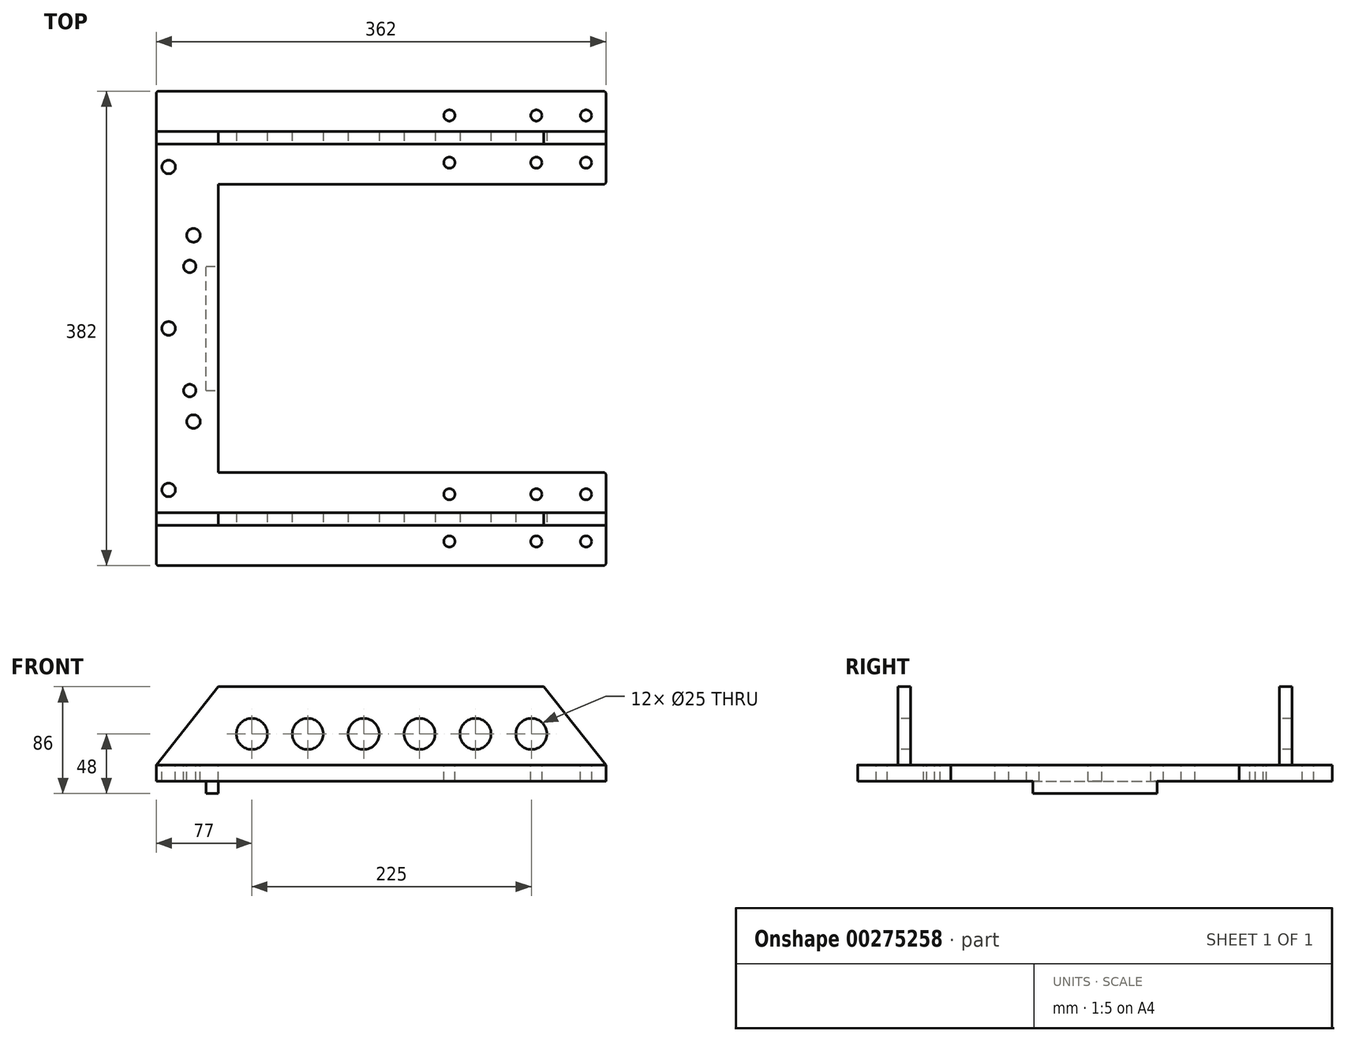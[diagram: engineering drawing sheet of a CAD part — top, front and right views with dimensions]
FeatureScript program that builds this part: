
annotation { "Feature Type Name" : "Feature", "Feature Type Description" : "" }
export const myFeature = defineFeature(function(context is Context, id is Id, definition is map)
    precondition{}
    {
        {
            var Q0;
            Q0=qCreatedBy(makeId("Top.planeOp"),FACE);
            var sketch = newSketch(context, id + "F0", { "sketchPlane" : qUnion([Q0])});
            skLineSegment(sketch, "E0", {"start": v(-299.03, 0) * mm, "end": v(319.03, 0) * mm, "construction": true});
            skLineSegment(sketch, "E1", {"start": v(0, 0) * mm, "end": v(0, 191) * mm});
            skLineSegment(sketch, "E2", {"start": v(0, 191) * mm, "end": v(362, 191) * mm});
            skLineSegment(sketch, "E3", {"start": v(362, 191) * mm, "end": v(362, 116) * mm});
            skLineSegment(sketch, "E4", {"start": v(362, 116) * mm, "end": v(0, 116) * mm});
            skLineSegment(sketch, "E5", {"start": v(50, 116) * mm, "end": v(50, 0) * mm});
            skLineSegment(sketch, "E6.MirrorCS", {"start": v(50, -116) * mm, "end": v(50, 0) * mm});
            skLineSegment(sketch, "E7.MirrorCS", {"start": v(0, 0) * mm, "end": v(0, -191) * mm});
            skLineSegment(sketch, "E8.MirrorCS", {"start": v(362, -116) * mm, "end": v(0, -116) * mm});
            skLineSegment(sketch, "E9.MirrorCS", {"start": v(0, -191) * mm, "end": v(362, -191) * mm});
            skLineSegment(sketch, "E10.MirrorCS", {"start": v(362, -191) * mm, "end": v(362, -116) * mm});
            skLineSegment(sketch, "E11", {"start": v(0, 158.5) * mm, "end": v(362, 158.5) * mm});
            skLineSegment(sketch, "E12", {"start": v(362, 148.5) * mm, "end": v(0, 148.5) * mm});
            skLineSegment(sketch, "E13.MirrorCS", {"start": v(362, -148.5) * mm, "end": v(0, -148.5) * mm});
            skLineSegment(sketch, "E14.MirrorCS", {"start": v(0, -158.5) * mm, "end": v(362, -158.5) * mm});
            skLineSegment(sketch, "E15", {"start": v(203.3, 171.5) * mm, "end": v(356.7, 171.5) * mm, "construction": true});
            skLineSegment(sketch, "E16", {"start": v(204.86, 133.5) * mm, "end": v(355.04, 133.5) * mm, "construction": true});
            skPoint(sketch, "E17", {"position": v(236, 171.5) * mm});
            skPoint(sketch, "E18", {"position": v(236, 133.5) * mm});
            skPoint(sketch, "E19", {"position": v(306, 171.5) * mm});
            skPoint(sketch, "E20", {"position": v(306, 133.5) * mm});
            skPoint(sketch, "E21", {"position": v(346, 171.5) * mm});
            skPoint(sketch, "E22", {"position": v(346, 133.5) * mm});
            skPoint(sketch, "E23", {"position": v(10, 130) * mm});
            skPoint(sketch, "E24", {"position": v(30, 75) * mm});
            skPoint(sketch, "E25", {"position": v(27, 50) * mm});
            skPoint(sketch, "E26", {"position": v(10, 0) * mm});
            skLineSegment(sketch, "E27", {"start": v(40, 0) * mm, "end": v(40, 50) * mm});
            skLineSegment(sketch, "E28", {"start": v(40, 50) * mm, "end": v(50, 50) * mm});
            skPoint(sketch, "E29.MirrorP", {"position": v(236, -171.5) * mm});
            skPoint(sketch, "E30.MirrorP", {"position": v(236, -133.5) * mm});
            skPoint(sketch, "E31.MirrorP", {"position": v(306, -171.5) * mm});
            skPoint(sketch, "E32.MirrorP", {"position": v(306, -133.5) * mm});
            skPoint(sketch, "E33.MirrorP", {"position": v(346, -171.5) * mm});
            skPoint(sketch, "E34.MirrorP", {"position": v(346, -133.5) * mm});
            skLineSegment(sketch, "E35.MirrorCS", {"start": v(40, 0) * mm, "end": v(40, -50) * mm});
            skPoint(sketch, "E36.MirrorP", {"position": v(27, -50) * mm});
            skLineSegment(sketch, "E37.MirrorCS", {"start": v(40, -50) * mm, "end": v(50, -50) * mm});
            skPoint(sketch, "E38.MirrorP", {"position": v(30, -75) * mm});
            skPoint(sketch, "E39.MirrorP", {"position": v(10, -130) * mm});
            skSolve(sketch);
        }
        {
            var Q0;
            Q0 = qSketchRegion(id + "F0", true);
            extrude(context, id + "F1", {"entities" : qUnion([Q0]), "oppositeDirection" : true, "depth" : 13 * mm});
        }
        {
            var Q0;
            Q0=makeQuery(id+"F0.imprint","IMPRINT",FACE,{"disambiguationData":[TD([[makeQuery(id+"F0.imprint","IMPRINT",EDGE,{"derivedFrom":sQuery(id+"F0.wireOp",EDGE,"E27")}),-1.0]])]});
            extrude(context, id + "F2", {"entities" : qUnion([Q0]), "operationType" : NewBodyOperationType.ADD, "oppositeDirection" : true, "depth" : (13 + 10) * mm});
        }
        {
            var Q0;
            {var subQ0=sQuery(id+"F0.wireOp",EDGE,"E11");Q0=makeQuery(id+"F0.imprint","IMPRINT",FACE,{"disambiguationData":[TD([[makeQuery(id+"F0.imprint","IMPRINT",EDGE,{"derivedFrom":subQ0}),-1.0]])]});}
            var Q1;
            {var subQ0=sQuery(id+"F0.wireOp",EDGE,"E13.MirrorCS");Q1=makeQuery(id+"F0.imprint","IMPRINT",FACE,{"disambiguationData":[TD([[makeQuery(id+"F0.imprint","IMPRINT",EDGE,{"derivedFrom":subQ0}),1.0]])]});}
            extrude(context, id + "F3", {"entities" : qUnion([Q0, Q1]), "operationType" : NewBodyOperationType.ADD, "depth" : 63 * mm});
        }
        {
            var Q0;
            Q0=sQuery(id+"F0.wireOp",VERTEX,"E17");
            var Q1;
            Q1=sQuery(id+"F0.wireOp",VERTEX,"E19");
            var Q2;
            Q2=sQuery(id+"F0.wireOp",VERTEX,"E21");
            var Q3;
            Q3=sQuery(id+"F0.wireOp",VERTEX,"E18");
            var Q4;
            Q4=sQuery(id+"F0.wireOp",VERTEX,"E20");
            var Q5;
            Q5=sQuery(id+"F0.wireOp",VERTEX,"E22");
            var Q6;
            Q6=sQuery(id+"F0.wireOp",VERTEX,"E29.MirrorP");
            var Q7;
            Q7=sQuery(id+"F0.wireOp",VERTEX,"E31.MirrorP");
            var Q8;
            Q8=sQuery(id+"F0.wireOp",VERTEX,"E33.MirrorP");
            var Q9;
            Q9=sQuery(id+"F0.wireOp",VERTEX,"E30.MirrorP");
            var Q10;
            Q10=sQuery(id+"F0.wireOp",VERTEX,"E32.MirrorP");
            var Q11;
            Q11=sQuery(id+"F0.wireOp",VERTEX,"E34.MirrorP");
            var Q12;
            Q12=makeQuery(id+"F1.opExtrude","SWEPT_BODY",BODY,{"disambiguationData":[OSD([sQuery(id+"F0.wireOp",EDGE,"E1"),sQuery(id+"F0.wireOp",EDGE,"E2"),sQuery(id+"F0.wireOp",EDGE,"E3"),sQuery(id+"F0.wireOp",EDGE,"E4"),sQuery(id+"F0.wireOp",EDGE,"E5"),sQuery(id+"F0.wireOp",EDGE,"E6.MirrorCS"),sQuery(id+"F0.wireOp",EDGE,"E7.MirrorCS"),sQuery(id+"F0.wireOp",EDGE,"E8.MirrorCS"),sQuery(id+"F0.wireOp",EDGE,"E9.MirrorCS"),sQuery(id+"F0.wireOp",EDGE,"E10.MirrorCS")])]});
            hole(context, id + "F4", {"style" : HoleStyle.SIMPLE, "endStyle" : HoleEndStyle.THROUGH, "holeDiameter" : 9 * mm, "tappedDepth" : 19.25 * mm, "tapClearance" : 3, "startFromSketch" : true, "locations" : qUnion([Q0, Q1, Q2, Q3, Q4, Q5, Q6, Q7, Q8, Q9, Q10, Q11]), "scope" : qUnion([Q12])});
        }
        {
            var Q0;
            Q0=sQuery(id+"F0.wireOp",VERTEX,"E23");
            var Q1;
            Q1=sQuery(id+"F0.wireOp",VERTEX,"E24");
            var Q2;
            Q2=sQuery(id+"F0.wireOp",VERTEX,"E39.MirrorP");
            var Q3;
            Q3=sQuery(id+"F0.wireOp",VERTEX,"E26");
            var Q4;
            Q4=sQuery(id+"F0.wireOp",VERTEX,"E38.MirrorP");
            var Q5;
            Q5=makeQuery(id+"F1.opExtrude","SWEPT_BODY",BODY,{"disambiguationData":[OSD([sQuery(id+"F0.wireOp",EDGE,"E1"),sQuery(id+"F0.wireOp",EDGE,"E2"),sQuery(id+"F0.wireOp",EDGE,"E3"),sQuery(id+"F0.wireOp",EDGE,"E4"),sQuery(id+"F0.wireOp",EDGE,"E5"),sQuery(id+"F0.wireOp",EDGE,"E6.MirrorCS"),sQuery(id+"F0.wireOp",EDGE,"E7.MirrorCS"),sQuery(id+"F0.wireOp",EDGE,"E8.MirrorCS"),sQuery(id+"F0.wireOp",EDGE,"E9.MirrorCS"),sQuery(id+"F0.wireOp",EDGE,"E10.MirrorCS")])]});
            hole(context, id + "F5", {"style" : HoleStyle.SIMPLE, "endStyle" : HoleEndStyle.THROUGH, "holeDiameter" : 11 * mm, "tappedDepth" : 19.25 * mm, "tapClearance" : 3, "startFromSketch" : true, "locations" : qUnion([Q0, Q1, Q2, Q3, Q4]), "scope" : qUnion([Q5])});
        }
        {
            var Q0;
            Q0=sQuery(id+"F0.wireOp",VERTEX,"E25");
            var Q1;
            Q1=sQuery(id+"F0.wireOp",VERTEX,"E36.MirrorP");
            var Q2;
            Q2=makeQuery(id+"F1.opExtrude","SWEPT_BODY",BODY,{"disambiguationData":[OSD([sQuery(id+"F0.wireOp",EDGE,"E1"),sQuery(id+"F0.wireOp",EDGE,"E2"),sQuery(id+"F0.wireOp",EDGE,"E3"),sQuery(id+"F0.wireOp",EDGE,"E4"),sQuery(id+"F0.wireOp",EDGE,"E5"),sQuery(id+"F0.wireOp",EDGE,"E6.MirrorCS"),sQuery(id+"F0.wireOp",EDGE,"E7.MirrorCS"),sQuery(id+"F0.wireOp",EDGE,"E8.MirrorCS"),sQuery(id+"F0.wireOp",EDGE,"E9.MirrorCS"),sQuery(id+"F0.wireOp",EDGE,"E10.MirrorCS")])]});
            hole(context, id + "F6", {"style" : HoleStyle.SIMPLE, "endStyle" : HoleEndStyle.THROUGH, "holeDiameter" : 10 * mm, "tappedDepth" : 19.25 * mm, "tapClearance" : 3, "startFromSketch" : true, "locations" : qUnion([Q0, Q1]), "scope" : qUnion([Q2])});
        }
        {
            var Q0;
            Q0=makeQuery(id+"F3.opExtrude","SWEPT_FACE",FACE,{"disambiguationData":[OSD([sQuery(id+"F0.wireOp",EDGE,"E14.MirrorCS")])]});
            var sketch = newSketch(context, id + "F7", { "sketchPlane" : qUnion([Q0])});
            skPoint(sketch, "E40", {"position": v(50, 63) * mm});
            skLineSegment(sketch, "E41.0", {"start": v(0, 63) * mm, "end": v(0, 0) * mm});
            skLineSegment(sketch, "E42.0", {"start": v(0, 63) * mm, "end": v(50, 63) * mm});
            skPoint(sketch, "E43.orphan", {"position": v(362, 63) * mm});
            skLineSegment(sketch, "E44", {"start": v(0, 0) * mm, "end": v(50, 63) * mm});
            skPoint(sketch, "E45", {"position": v(312, 63) * mm});
            skLineSegment(sketch, "E46", {"start": v(362, 0) * mm, "end": v(312, 63) * mm});
            skLineSegment(sketch, "E47.0", {"start": v(362, 63) * mm, "end": v(362, 0) * mm});
            skLineSegment(sketch, "E48.trimOffspring", {"start": v(312, 63) * mm, "end": v(362, 63) * mm});
            skLineSegment(sketch, "E49", {"start": v(-34.34, 25) * mm, "end": v(392.45, 25) * mm, "construction": true});
            skLineSegment(sketch, "E50.0", {"start": v(0, -13) * mm, "end": v(362, -13) * mm, "construction": true});
            skPoint(sketch, "E51", {"position": v(77, 25) * mm});
            skPoint(sketch, "E52", {"position": v(122, 25) * mm});
            skPoint(sketch, "E53", {"position": v(167, 25) * mm});
            skPoint(sketch, "E54", {"position": v(212, 25) * mm});
            skPoint(sketch, "E55", {"position": v(257, 25) * mm});
            skPoint(sketch, "E56", {"position": v(302, 25) * mm});
            skSolve(sketch);
        }
        {
            var Q0;
            Q0=makeQuery(id+"F7.imprint","IMPRINT",FACE,{"disambiguationData":[TD([[makeQuery(id+"F7.imprint","IMPRINT",EDGE,{"derivedFrom":sQuery(id+"F7.wireOp",EDGE,"E41.0")}),1.0]])]});
            var Q1;
            Q1=makeQuery(id+"F7.imprint","IMPRINT",FACE,{"disambiguationData":[TD([[makeQuery(id+"F7.imprint","IMPRINT",EDGE,{"derivedFrom":sQuery(id+"F7.wireOp",EDGE,"E46")}),-1.0]])]});
            extrude(context, id + "F8", {"entities" : qUnion([Q0, Q1]), "operationType" : NewBodyOperationType.REMOVE, "endBound" : BoundingType.THROUGH_ALL, "oppositeDirection" : true, "depth" : 25 * mm});
        }
        {
            var Q0;
            Q0=sQuery(id+"F7.wireOp",VERTEX,"E51");
            var Q1;
            Q1=sQuery(id+"F7.wireOp",VERTEX,"E52");
            var Q2;
            Q2=sQuery(id+"F7.wireOp",VERTEX,"E53");
            var Q3;
            Q3=sQuery(id+"F7.wireOp",VERTEX,"E54");
            var Q4;
            Q4=sQuery(id+"F7.wireOp",VERTEX,"E55");
            var Q5;
            Q5=sQuery(id+"F7.wireOp",VERTEX,"E56");
            var Q6;
            Q6=makeQuery(id+"F1.opExtrude","SWEPT_BODY",BODY,{"disambiguationData":[OSD([sQuery(id+"F0.wireOp",EDGE,"E1"),sQuery(id+"F0.wireOp",EDGE,"E2"),sQuery(id+"F0.wireOp",EDGE,"E3"),sQuery(id+"F0.wireOp",EDGE,"E4"),sQuery(id+"F0.wireOp",EDGE,"E5"),sQuery(id+"F0.wireOp",EDGE,"E6.MirrorCS"),sQuery(id+"F0.wireOp",EDGE,"E7.MirrorCS"),sQuery(id+"F0.wireOp",EDGE,"E8.MirrorCS"),sQuery(id+"F0.wireOp",EDGE,"E9.MirrorCS"),sQuery(id+"F0.wireOp",EDGE,"E10.MirrorCS")])]});
            hole(context, id + "F9", {"style" : HoleStyle.SIMPLE, "endStyle" : HoleEndStyle.THROUGH, "holeDiameter" : 25 * mm, "tappedDepth" : 19.25 * mm, "tapClearance" : 3, "startFromSketch" : true, "locations" : qUnion([Q0, Q1, Q2, Q3, Q4, Q5]), "scope" : qUnion([Q6])});
        }
        {
            var Q0;
            Q0=makeQuery(id+"F1.opExtrude","SWEPT_EDGE",EDGE,{"disambiguationData":[OSD([sQuery(id+"F0.wireOp",EDGE,"E9.MirrorCS"),sQuery(id+"F0.wireOp",EDGE,"E10.MirrorCS")])]});
            var Q1;
            Q1=makeQuery(id+"F1.opExtrude","SWEPT_EDGE",EDGE,{"disambiguationData":[OSD([sQuery(id+"F0.wireOp",EDGE,"E3"),sQuery(id+"F0.wireOp",EDGE,"E4")])]});
            var Q2;
            Q2=makeQuery(id+"F1.opExtrude","SWEPT_EDGE",EDGE,{"disambiguationData":[OSD([sQuery(id+"F0.wireOp",EDGE,"E8.MirrorCS"),sQuery(id+"F0.wireOp",EDGE,"E10.MirrorCS")])]});
            var Q3;
            Q3=makeQuery(id+"F1.opExtrude","SWEPT_EDGE",EDGE,{"disambiguationData":[OSD([sQuery(id+"F0.wireOp",EDGE,"E2"),sQuery(id+"F0.wireOp",EDGE,"E3")])]});
            var Q4;
            Q4=makeQuery(id+"F1.opExtrude","SWEPT_EDGE",EDGE,{"disambiguationData":[OSD([sQuery(id+"F0.wireOp",EDGE,"E7.MirrorCS"),sQuery(id+"F0.wireOp",EDGE,"E9.MirrorCS")])]});
            var Q5;
            Q5=makeQuery(id+"F1.opExtrude","SWEPT_EDGE",EDGE,{"disambiguationData":[OSD([sQuery(id+"F0.wireOp",EDGE,"E1"),sQuery(id+"F0.wireOp",EDGE,"E2")])]});
            fillet(context, id + "F10", {"entities" : qUnion([Q0, Q1, Q2, Q3, Q4, Q5]), "radius" : 2 * mm, "tangentPropagation" : true, "allowEdgeOverflow" : false});
        }
    });
